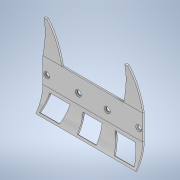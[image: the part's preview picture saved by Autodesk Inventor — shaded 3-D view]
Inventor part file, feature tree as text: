
AUTODESK INVENTOR PART (.ipt)
format: ipt  version: 2021 (Build 250183000, 183)  size: 262,144 bytes
history: native  units: mm
features: other x9, sketch x5, sheet_metal_op x1, hole x1
ambient origin geometry x8: Origin, YZ Plane, XZ Plane, XY Plane, X Axis, Y Axis, Z Axis, Center Point
bodies: Body1 (feature_tree)
feature tree (16):
  other  "Sólido1"
  sheet_metal_op  "Face1"
  other  "Dobra1"
  other  "Dobra2"
  hole  "Furo1"  [1 undecoded]
  sketch  "Esboço1"  dims[d0=100.0mm d1=90.0mm]
  other  "Placa1"
  sketch  "Esboço2"  dims[d2=1.5mm]
  sketch  "Esboço3"  dims[d3=19.0mm]
  other  "Contorno projetado1"
  sketch  "Esboço5"  dims[d4=18.0mm]
  sketch  "Esboço6"  dims[d5=2.0mm d6=15.0deg d7=2.446mm d8=20.227mm d9=1.5mm d10=0.0mm d11=1.5mm d12=0.75mm d13=3.0mm d14=1.5mm d15=6.361725mm d16=36.683mm d19=25.0mm d25=1.5mm d26=0.75mm d27=3.0mm d28=1.5mm d29=4.363323mm d30=120.0mm d31=10.0mm d32=4.0mm d33=4.0mm d34=14.5mm d35=14.5mm d36=4.0mm d37=6.0mm d38=6.0mm d39=2.0mm d40=90.0deg d41=1.5mm d42=0.0mm d46=3.0mm d47=8.0mm d48=8.0mm d49=8.0mm d50=3.0mm d51=8.0mm d52=1.5mm d53=0.0mm]
  other  "Contorno projetado5"
  other  "Contorno projetado7"
  other  "Recortar1"
  other  "Recortar3"
note: 1 required parameter value undecoded (feature->parameter linkage not recoverable at this tier; creation-order binding heuristic only, values carry confidence <= 0.55)
